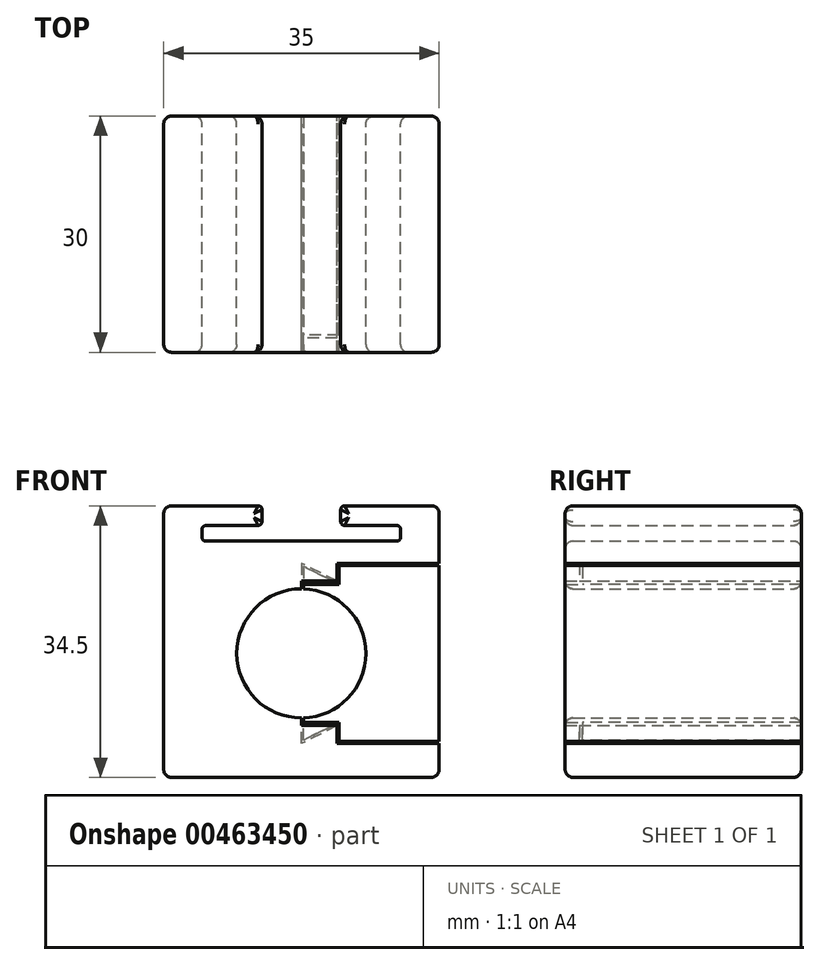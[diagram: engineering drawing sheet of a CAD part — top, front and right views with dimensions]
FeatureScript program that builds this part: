
annotation { "Feature Type Name" : "Feature", "Feature Type Description" : "" }
export const myFeature = defineFeature(function(context is Context, id is Id, definition is map)
    precondition{}
    {
        {
            var Q0;
            Q0=qCreatedBy(makeId("Front.planeOp"),FACE);
            var sketch = newSketch(context, id + "F0", { "sketchPlane" : qUnion([Q0])});
            skLineSegment(sketch, "E0.bottom", {"start": v(16.51, -15.75) * mm, "end": v(-16.49, -15.75) * mm});
            skLineSegment(sketch, "E0.top", {"start": v(16.51, 18.75) * mm, "end": v(5.5, 18.75) * mm});
            skLineSegment(sketch, "E0.left", {"start": v(17.51, -14.75) * mm, "end": v(17.51, -11.45) * mm});
            skLineSegment(sketch, "E0.right", {"start": v(-17.49, -14.75) * mm, "end": v(-17.49, 17.75) * mm});
            skPoint(sketch, "E1.middle", {"position": v(0, 0) * mm});
            skLineSegment(sketch, "E2.left", {"start": v(-5, 16.75) * mm, "end": v(-5, 18.25) * mm});
            skLineSegment(sketch, "E2.right", {"start": v(5, 16.75) * mm, "end": v(5, 18.25) * mm});
            skPoint(sketch, "E2.middle.positionSnap0", {"position": v(0.01, 18.75) * mm});
            skPoint(sketch, "E2.centerSnap0", {"position": v(0.01, 18.75) * mm});
            skLineSegment(sketch, "E3.bottom", {"start": v(12.1, 14.25) * mm, "end": v(10.29, 14.25) * mm});
            skLineSegment(sketch, "E3.top", {"start": v(12.1, 16.25) * mm, "end": v(5.5, 16.25) * mm});
            skLineSegment(sketch, "E3.left", {"start": v(12.6, 14.75) * mm, "end": v(12.6, 15.75) * mm});
            skLineSegment(sketch, "E3.right", {"start": v(-12.6, 14.75) * mm, "end": v(-12.6, 15.75) * mm});
            skPoint(sketch, "E3.middle", {"position": v(0, 15.25) * mm});
            skPoint(sketch, "E4.visualSharp", {"position": v(-12.6, 16.25) * mm});
            skArc(sketch, "E4.filletArc", {"start": v(-12.1, 16.25) * mm, "mid": v(-12.46, 16.1) * mm, "end": v(-12.6, 15.75) * mm});
            skPoint(sketch, "E5.visualSharp", {"position": v(12.6, 16.25) * mm});
            skArc(sketch, "E5.filletArc", {"start": v(12.6, 15.75) * mm, "mid": v(12.46, 16.1) * mm, "end": v(12.1, 16.25) * mm});
            skLineSegment(sketch, "E6.trimOffspring", {"start": v(-5.5, 18.75) * mm, "end": v(-16.49, 18.75) * mm});
            skLineSegment(sketch, "E7.trimOffspring", {"start": v(-5.5, 16.25) * mm, "end": v(-12.1, 16.25) * mm});
            skPoint(sketch, "E8.visualSharp", {"position": v(-12.6, 14.25) * mm});
            skArc(sketch, "E8.filletArc", {"start": v(-12.6, 14.75) * mm, "mid": v(-12.46, 14.4) * mm, "end": v(-12.1, 14.25) * mm});
            skPoint(sketch, "E9.visualSharp", {"position": v(-5, 16.25) * mm});
            skArc(sketch, "E9.filletArc", {"start": v(-5.5, 16.25) * mm, "mid": v(-5.15, 16.4) * mm, "end": v(-5, 16.75) * mm});
            skPoint(sketch, "E10.visualSharp", {"position": v(-5, 18.75) * mm});
            skArc(sketch, "E10.filletArc", {"start": v(-5, 18.25) * mm, "mid": v(-5.15, 18.6) * mm, "end": v(-5.5, 18.75) * mm});
            skPoint(sketch, "E11.visualSharp", {"position": v(5, 18.75) * mm});
            skArc(sketch, "E11.filletArc", {"start": v(5.5, 18.75) * mm, "mid": v(5.15, 18.6) * mm, "end": v(5, 18.25) * mm});
            skPoint(sketch, "E12.visualSharp", {"position": v(5, 16.25) * mm});
            skArc(sketch, "E12.filletArc", {"start": v(5, 16.75) * mm, "mid": v(5.15, 16.4) * mm, "end": v(5.5, 16.25) * mm});
            skPoint(sketch, "E13.visualSharp", {"position": v(-17.49, 18.75) * mm});
            skArc(sketch, "E13.filletArc", {"start": v(-16.49, 18.75) * mm, "mid": v(-17.2, 18.46) * mm, "end": v(-17.49, 17.75) * mm});
            skPoint(sketch, "E14.visualSharp", {"position": v(17.51, 18.75) * mm});
            skArc(sketch, "E14.filletArc", {"start": v(17.51, 17.75) * mm, "mid": v(17.22, 18.46) * mm, "end": v(16.51, 18.75) * mm});
            skPoint(sketch, "E15.visualSharp", {"position": v(12.6, 14.25) * mm});
            skArc(sketch, "E15.filletArc", {"start": v(12.1, 14.25) * mm, "mid": v(12.46, 14.4) * mm, "end": v(12.6, 14.75) * mm});
            skPoint(sketch, "E16.visualSharp", {"position": v(-17.49, -15.75) * mm});
            skArc(sketch, "E16.filletArc", {"start": v(-17.49, -14.75) * mm, "mid": v(-17.2, -15.46) * mm, "end": v(-16.49, -15.75) * mm});
            skPoint(sketch, "E17.visualSharp", {"position": v(17.51, -15.75) * mm});
            skArc(sketch, "E17.filletArc", {"start": v(16.51, -15.75) * mm, "mid": v(17.22, -15.46) * mm, "end": v(17.51, -14.75) * mm});
            skLineSegment(sketch, "E18.3", {"start": v(0, -11.45) * mm, "end": v(0, 0) * mm});
            skLineSegment(sketch, "E18.4", {"start": v(4.56, -9.17) * mm, "end": v(0, -11.45) * mm});
            skLineSegment(sketch, "E19.trimOffspring", {"start": v(17.51, -2.85) * mm, "end": v(17.51, 11.2) * mm});
            skLineSegment(sketch, "E20.trimOffspring", {"start": v(10.14, 14.25) * mm, "end": v(-12.1, 14.25) * mm});
            skLineSegment(sketch, "E21", {"start": v(4.56, -11.45) * mm, "end": v(17.51, -11.45) * mm});
            skCircle(sketch, "E22", {"center": v(0, 0) * mm, "radius": 8.2 * mm});
            skLineSegment(sketch, "E23.trimOffspring", {"start": v(17.51, 11.45) * mm, "end": v(17.51, 17.75) * mm});
            skLineSegment(sketch, "E24.trimOffspring", {"start": v(17.51, -11.2) * mm, "end": v(17.51, -2.85) * mm});
            skLineSegment(sketch, "E25", {"start": v(10.29, 14.25) * mm, "end": v(10.14, 14.25) * mm});
            skLineSegment(sketch, "E26", {"start": v(4.56, -9.17) * mm, "end": v(4.56, -11.45) * mm});
            skLineSegment(sketch, "E27.MirrorCS", {"start": v(0, 11.45) * mm, "end": v(0, 0) * mm});
            skLineSegment(sketch, "E28.MirrorCS", {"start": v(4.56, 9.17) * mm, "end": v(0, 11.45) * mm});
            skLineSegment(sketch, "E29.MirrorCS", {"start": v(4.56, 9.17) * mm, "end": v(4.56, 11.45) * mm});
            skLineSegment(sketch, "E30.MirrorCS", {"start": v(4.56, 11.45) * mm, "end": v(17.51, 11.45) * mm});
            skLineSegment(sketch, "E31.0", {"start": v(4.8, -11.2) * mm, "end": v(17.51, -11.2) * mm});
            skLineSegment(sketch, "E31.1", {"start": v(4.81, -8.77) * mm, "end": v(4.8, -11.2) * mm});
            skLineSegment(sketch, "E31.2", {"start": v(4.81, -8.77) * mm, "end": v(0.25, -11.05) * mm});
            skLineSegment(sketch, "E31.3", {"start": v(0.25, -11.05) * mm, "end": v(0.25, 0) * mm});
            skLineSegment(sketch, "E31.4", {"start": v(4.8, 11.2) * mm, "end": v(17.51, 11.2) * mm});
            skLineSegment(sketch, "E31.5", {"start": v(4.81, 8.77) * mm, "end": v(4.8, 11.2) * mm});
            skLineSegment(sketch, "E31.6", {"start": v(4.81, 8.77) * mm, "end": v(0.25, 11.05) * mm});
            skLineSegment(sketch, "E31.7", {"start": v(0.25, 11.05) * mm, "end": v(0.25, 0) * mm});
            skLineSegment(sketch, "E32", {"start": v(4.56, -9.17) * mm, "end": v(0, -9.16) * mm});
            skLineSegment(sketch, "E33", {"start": v(4.81, -8.77) * mm, "end": v(0.25, -8.76) * mm});
            skLineSegment(sketch, "E34", {"start": v(4.81, 8.77) * mm, "end": v(0.25, 8.77) * mm});
            skLineSegment(sketch, "E35", {"start": v(4.56, 9.17) * mm, "end": v(0, 9.17) * mm});
            skSolve(sketch);
        }
        {
            var Q0;
            Q0=makeQuery(id+"F0.imprint","IMPRINT",FACE,{"disambiguationData":[TD([[makeQuery(id+"F0.imprint","IMPRINT",EDGE,{"derivedFrom":sQuery(id+"F0.wireOp",EDGE,"E0.bottom")}),-1.0]])]});
            var Q1;
            {var subQ5=sQuery(id+"F0.wireOp",EDGE,"E19.trimOffspring");Q1=makeQuery(id+"F0.imprint","IMPRINT",FACE,{"disambiguationData":[TD([[makeQuery(id+"F0.imprint","IMPRINT",EDGE,{"derivedFrom":subQ5}),1.0]])]});}
            extrude(context, id + "F1", {"entities" : qUnion([Q0, Q1]), "depth" : 30 * mm, "offsetDistance" : 25 * mm, "symmetric" : true});
        }
        {
            var Q0;
            {var subQ8=sQuery(id+"F0.wireOp",EDGE,"E28.MirrorCS");Q0=makeQuery(id+"F0.imprint","IMPRINT",FACE,{"disambiguationData":[TD([[makeQuery(id+"F0.imprint","IMPRINT",EDGE,{"derivedFrom":subQ8}),1.0]])]});}
            var Q1;
            {var subQ0=sQuery(id+"F0.wireOp",EDGE,"E31.7");var subQ1=sQuery(id+"F0.wireOp",EDGE,"E31.6");var subQ2=makeQuery(id+"F0.imprint","INTERSECT",VERTEX,{"derivedFrom":[subQ1,subQ0]});Q1=makeQuery(id+"F0.imprint","IMPRINT",FACE,{"disambiguationData":[TD([[makeQuery(id+"F0.imprint","IMPRINT",EDGE,{"disambiguationData":[TD([[subQ2,1.0]])],"derivedFrom":subQ1}),1.0]])]});}
            var Q2;
            {var subQ0=sQuery(id+"F0.wireOp",EDGE,"E31.3");var subQ1=sQuery(id+"F0.wireOp",EDGE,"E31.2");var subQ2=makeQuery(id+"F0.imprint","INTERSECT",VERTEX,{"derivedFrom":[subQ1,subQ0]});Q2=makeQuery(id+"F0.imprint","IMPRINT",FACE,{"disambiguationData":[TD([[makeQuery(id+"F0.imprint","IMPRINT",EDGE,{"disambiguationData":[TD([[subQ2,1.0]])],"derivedFrom":subQ1}),-1.0]])]});}
            var Q3;
            {var subQ5=sQuery(id+"F0.wireOp",EDGE,"E18.4");Q3=makeQuery(id+"F0.imprint","IMPRINT",FACE,{"disambiguationData":[TD([[makeQuery(id+"F0.imprint","IMPRINT",EDGE,{"derivedFrom":subQ5}),-1.0]])]});}
            extrude(context, id + "F2", {"entities" : qUnion([Q0, Q1, Q2, Q3]), "operationType" : NewBodyOperationType.ADD, "depth" : 15 * mm, "hasSecondDirection" : true, "secondDirectionOppositeDirection" : false, "secondDirectionDepth" : 13.2 * mm, "offsetDistance" : 25 * mm});
        }
        {
            var Q0;
            {var subQ0=sQuery(id+"F0.wireOp",EDGE,"E34");Q0=makeQuery(id+"F0.imprint","IMPRINT",FACE,{"disambiguationData":[TD([[makeQuery(id+"F0.imprint","IMPRINT",EDGE,{"derivedFrom":subQ0}),-1.0]])]});}
            var Q1;
            {var subQ0=sQuery(id+"F0.wireOp",EDGE,"E31.7");var subQ1=sQuery(id+"F0.wireOp",EDGE,"E31.6");var subQ2=makeQuery(id+"F0.imprint","INTERSECT",VERTEX,{"derivedFrom":[subQ1,subQ0]});Q1=makeQuery(id+"F0.imprint","IMPRINT",FACE,{"disambiguationData":[TD([[makeQuery(id+"F0.imprint","IMPRINT",EDGE,{"disambiguationData":[TD([[subQ2,1.0]])],"derivedFrom":subQ1}),1.0]])]});}
            var Q2;
            {var subQ0=sQuery(id+"F0.wireOp",EDGE,"E33");Q2=makeQuery(id+"F0.imprint","IMPRINT",FACE,{"disambiguationData":[TD([[makeQuery(id+"F0.imprint","IMPRINT",EDGE,{"derivedFrom":subQ0}),1.0]])]});}
            var Q3;
            {var subQ0=sQuery(id+"F0.wireOp",EDGE,"E31.3");var subQ1=sQuery(id+"F0.wireOp",EDGE,"E31.2");var subQ2=makeQuery(id+"F0.imprint","INTERSECT",VERTEX,{"derivedFrom":[subQ1,subQ0]});Q3=makeQuery(id+"F0.imprint","IMPRINT",FACE,{"disambiguationData":[TD([[makeQuery(id+"F0.imprint","IMPRINT",EDGE,{"disambiguationData":[TD([[subQ2,1.0]])],"derivedFrom":subQ1}),-1.0]])]});}
            extrude(context, id + "F3", {"entities" : qUnion([Q0, Q1, Q2, Q3]), "operationType" : NewBodyOperationType.ADD, "depth" : -15 * mm, "hasSecondDirection" : true, "secondDirectionOppositeDirection" : false, "secondDirectionDepth" : 12.8 * mm});
        }
        {
            var Q0;
            Q0=makeQuery(id+"F1.opExtrude","CAP_EDGE",EDGE,{"disambiguationData":[OSD([sQuery(id+"F0.wireOp",EDGE,"E0.left")])],"isStart":false});
            var Q1;
            Q1=makeQuery(id+"F1.opExtrude","CAP_EDGE",EDGE,{"disambiguationData":[OSD([sQuery(id+"F0.wireOp",EDGE,"E19.trimOffspring"),sQuery(id+"F0.wireOp",EDGE,"E24.trimOffspring")])],"isStart":false});
            var Q2;
            Q2=makeQuery(id+"F1.opExtrude","CAP_EDGE",EDGE,{"disambiguationData":[OSD([sQuery(id+"F0.wireOp",EDGE,"E23.trimOffspring")])],"isStart":true});
            var Q3;
            Q3=makeQuery(id+"F1.opExtrude","CAP_EDGE",EDGE,{"disambiguationData":[OSD([sQuery(id+"F0.wireOp",EDGE,"E19.trimOffspring"),sQuery(id+"F0.wireOp",EDGE,"E24.trimOffspring")])],"isStart":true});
            var Q4;
            {var subQ0=sQuery(id+"F0.wireOp",EDGE,"E22");Q4=makeQuery(id+"F1.opExtrude","CAP_EDGE",EDGE,{"disambiguationData":[OSD([subQ0]),TDD([makeQuery(id+"F0.imprint","IMPRINT",EDGE,{"disambiguationData":[TD([[makeQuery(id+"F0.imprint","INTERSECT",VERTEX,{"derivedFrom":[subQ0,sQuery(id+"F0.wireOp",EDGE,"E31.7")]}),1.0]])],"derivedFrom":subQ0})])],"isStart":true});}
            var Q5;
            {var subQ0=sQuery(id+"F0.wireOp",EDGE,"E22");Q5=makeQuery(id+"F1.opExtrude","CAP_EDGE",EDGE,{"disambiguationData":[OSD([subQ0]),TDD([makeQuery(id+"F0.imprint","IMPRINT",EDGE,{"disambiguationData":[TD([[makeQuery(id+"F0.imprint","INTERSECT",VERTEX,{"derivedFrom":[sQuery(id+"F0.wireOp",EDGE,"E18.3"),subQ0]}),1.0]])],"derivedFrom":subQ0})])],"isStart":true});}
            var Q6;
            {var subQ0=sQuery(id+"F0.wireOp",EDGE,"E22");Q6=makeQuery(id+"F1.opExtrude","CAP_EDGE",EDGE,{"disambiguationData":[OSD([subQ0]),TDD([makeQuery(id+"F0.imprint","IMPRINT",EDGE,{"disambiguationData":[TD([[makeQuery(id+"F0.imprint","INTERSECT",VERTEX,{"derivedFrom":[subQ0,sQuery(id+"F0.wireOp",EDGE,"E31.7")]}),1.0]])],"derivedFrom":subQ0})])],"isStart":false});}
            var Q7;
            {var subQ0=sQuery(id+"F0.wireOp",EDGE,"E22");Q7=makeQuery(id+"F1.opExtrude","CAP_EDGE",EDGE,{"disambiguationData":[OSD([subQ0]),TDD([makeQuery(id+"F0.imprint","IMPRINT",EDGE,{"disambiguationData":[TD([[makeQuery(id+"F0.imprint","INTERSECT",VERTEX,{"derivedFrom":[sQuery(id+"F0.wireOp",EDGE,"E18.3"),subQ0]}),1.0]])],"derivedFrom":subQ0})])],"isStart":false});}
            fillet(context, id + "F4", {"entities" : qUnion([Q0, Q1, Q2, Q3, Q4, Q5, Q6, Q7]), "radius" : 1 * mm, "tangentPropagation" : true, "allowEdgeOverflow" : false});
        }
    });
